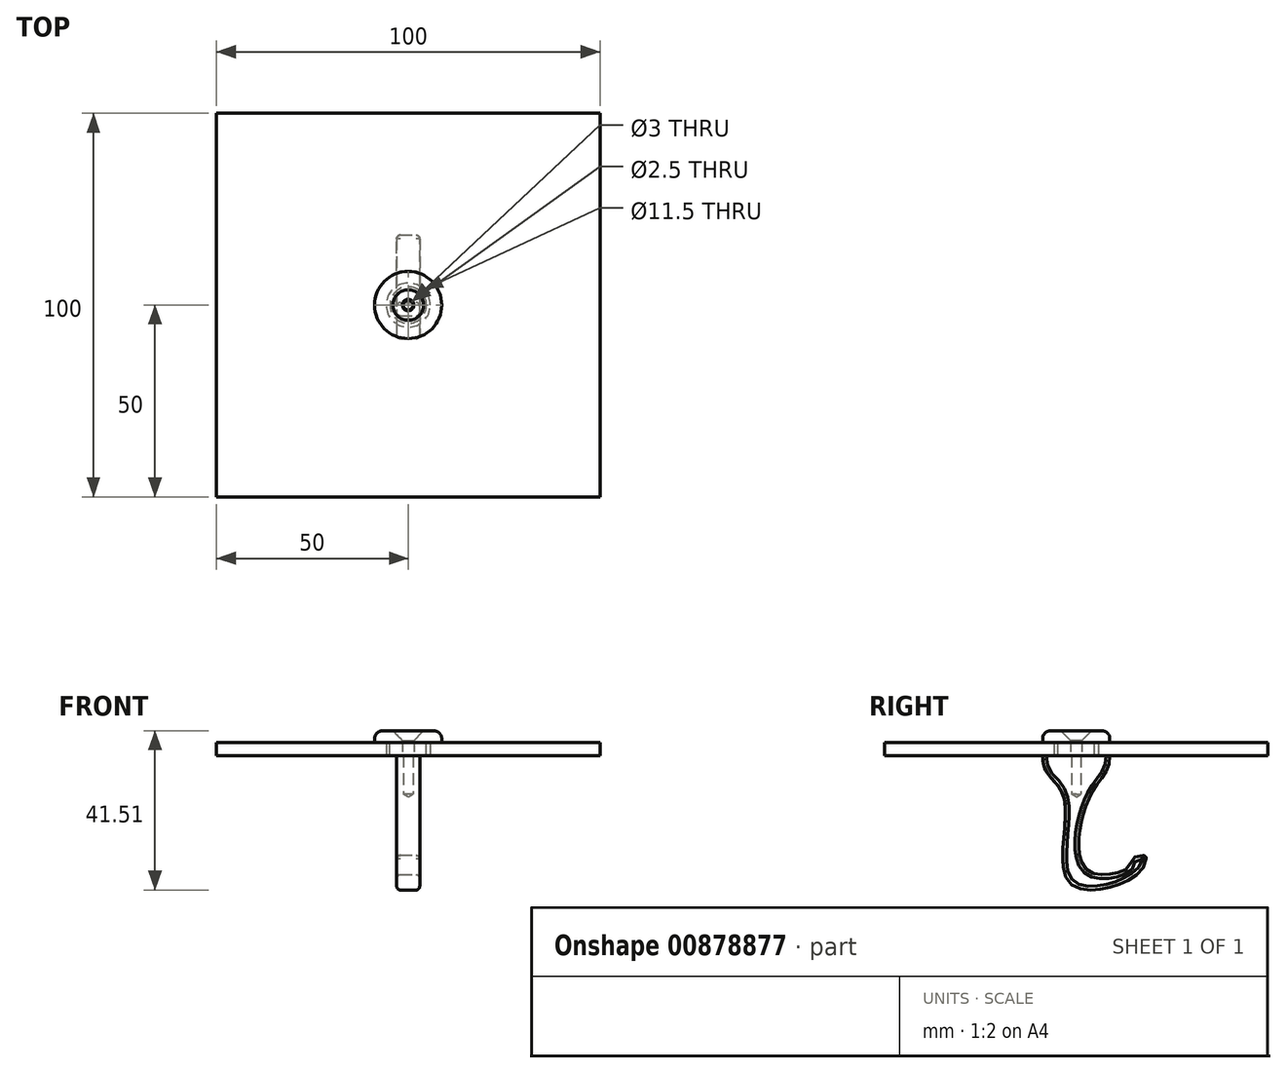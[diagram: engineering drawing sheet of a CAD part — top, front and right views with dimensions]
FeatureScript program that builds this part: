
annotation { "Feature Type Name" : "Feature", "Feature Type Description" : "" }
export const myFeature = defineFeature(function(context is Context, id is Id, definition is map)
    precondition{}
    {
        {
            var Q0;
            Q0=qCreatedBy(makeId("Top.planeOp"),FACE);
            var sketch = newSketch(context, id + "F0", { "sketchPlane" : qUnion([Q0])});
            skLineSegment(sketch, "E0.bottom", {"start": v(50, -50) * mm, "end": v(-50, -50) * mm});
            skLineSegment(sketch, "E0.top", {"start": v(50, 50) * mm, "end": v(-50, 50) * mm});
            skLineSegment(sketch, "E0.left", {"start": v(50, -50) * mm, "end": v(50, 50) * mm});
            skLineSegment(sketch, "E0.right", {"start": v(-50, -50) * mm, "end": v(-50, 50) * mm});
            skPoint(sketch, "E0.middle", {"position": v(0, 0) * mm});
            skCircle(sketch, "E1", {"center": v(0, 0) * mm, "radius": 5.75 * mm});
            skSolve(sketch);
        }
        {
            var Q0;
            Q0=makeQuery(id+"F0.imprint","IMPRINT",FACE,{"disambiguationData":[TD([[makeQuery(id+"F0.imprint","IMPRINT",EDGE,{"derivedFrom":sQuery(id+"F0.wireOp",EDGE,"E0.bottom")}),-1.0]])]});
            extrude(context, id + "F1", {"entities" : qUnion([Q0]), "depth" : 3.5 * mm, "offsetDistance" : 25 * mm});
        }
        {
            var Q0;
            Q0=makeQuery(id+"F1.opExtrude","CAP_FACE",FACE,{"disambiguationData":[OSD([sQuery(id+"F0.wireOp",EDGE,"E0.bottom"),sQuery(id+"F0.wireOp",EDGE,"E0.top"),sQuery(id+"F0.wireOp",EDGE,"E0.left"),sQuery(id+"F0.wireOp",EDGE,"E0.right"),sQuery(id+"F0.wireOp",EDGE,"E1")])],"isStart":false});
            var sketch = newSketch(context, id + "F2", { "sketchPlane" : qUnion([Q0])});
            skCircle(sketch, "E2", {"center": v(0, 0) * mm, "radius": 8.75 * mm});
            skSolve(sketch);
        }
        {
            var Q0;
            Q0=makeQuery(id+"F2.imprint","IMPRINT",FACE,{"disambiguationData":[TD([[makeQuery(id+"F2.imprint","IMPRINT",EDGE,{"derivedFrom":sQuery(id+"F2.wireOp",EDGE,"E2")}),1.0]])]});
            var Q1;
            Q1=makeQuery(id+"F2.imprint","IMPRINT",FACE,{"disambiguationData":[TD([[makeQuery(id+"F2.imprint","IMPRINT",EDGE,{"derivedFrom":makeQuery(id+"F1.opExtrude","CAP_EDGE",EDGE,{"disambiguationData":[OSD([sQuery(id+"F0.wireOp",EDGE,"E1")])],"isStart":false})}),1.0]])]});
            extrude(context, id + "F3", {"entities" : qUnion([Q0, Q1]), "depth" : 3 * mm, "offsetDistance" : 25 * mm});
        }
        {
            var Q0;
            Q0=makeQuery(id+"F3.opExtrude","CAP_FACE",FACE,{"disambiguationData":[OSD([sQuery(id+"F2.wireOp",EDGE,"E2")])],"isStart":true});
            var sketch = newSketch(context, id + "F4", { "sketchPlane" : qUnion([Q0])});
            skCircle(sketch, "E3.0", {"center": v(0, 0) * mm, "radius": 4.75 * mm});
            skSolve(sketch);
        }
        {
            var Q0;
            Q0=makeQuery(id+"F4.imprint","IMPRINT",FACE,{"disambiguationData":[TD([[makeQuery(id+"F4.imprint","IMPRINT",EDGE,{"derivedFrom":sQuery(id+"F4.wireOp",EDGE,"E3.0")}),1.0]])]});
            extrude(context, id + "F5", {"entities" : qUnion([Q0]), "operationType" : NewBodyOperationType.ADD, "depth" : 3.3 * mm, "offsetDistance" : 25 * mm});
        }
        {
            var Q0;
            Q0=makeQuery(id+"F3.opExtrude","CAP_EDGE",EDGE,{"disambiguationData":[OSD([sQuery(id+"F2.wireOp",EDGE,"E2")])],"isStart":false});
            fillet(context, id + "F6", {"entities" : qUnion([Q0]), "radius" : 2 * mm, "tangentPropagation" : true, "allowEdgeOverflow" : false});
        }
        {
            var Q0;
            Q0=makeQuery(id+"F3.opExtrude","CAP_FACE",FACE,{"disambiguationData":[OSD([sQuery(id+"F2.wireOp",EDGE,"E2")])],"isStart":false});
            var sketch = newSketch(context, id + "F7", { "sketchPlane" : qUnion([Q0])});
            skPoint(sketch, "E4", {"position": v(0, 0) * mm});
            skSolve(sketch);
        }
        {
            var Q0;
            Q0=sQuery(id+"F7.wireOp",VERTEX,"E4");
            var Q1;
            Q1=makeQuery(id+"F3.opExtrude","SWEPT_BODY",BODY,{"disambiguationData":[OSD([sQuery(id+"F2.wireOp",EDGE,"E2")])]});
            hole(context, id + "F8", {"style" : HoleStyle.C_SINK, "endStyle" : HoleEndStyle.THROUGH, "holeDiameter" : 3 * mm, "cSinkDiameter" : 8 * mm, "cSinkAngle" : 90 * degree, "majorDiameter" : 5 * mm, "isTappedThrough" : true, "tappedDepth" : 12 * mm, "tapClearance" : 3, "locations" : qUnion([Q0]), "scope" : qUnion([Q1]), "startStyle" : HoleStartStyle.SKETCH});
        }
        {
            var Q0;
            Q0=qCreatedBy(makeId("Right.planeOp"),FACE);
            var sketch = newSketch(context, id + "F9", { "sketchPlane" : qUnion([Q0])});
            skLineSegment(sketch, "E5", {"start": v(8.75, 0) * mm, "end": v(-8.75, 0) * mm});
            skLineSegment(sketch, "E6.0", {"start": v(-8.75, 3.5) * mm, "end": v(8.75, 3.5) * mm, "construction": true});
            skFitSpline(sketch, "E7", {"points": [v(8.75, 0) * mm, v(7.3, -4.9) * mm, v(2.97, -12) * mm, v(2.97, -29.9) * mm, v(13.79, -28.94) * mm, v(14.4, -27.1) * mm, v(17.8, -26.07) * mm, v(16.15, -30.66) * mm, v(-1.6, -33.27) * mm, v(-2.97, -12) * mm, v(-7.3, -4.9) * mm, v(-8.75, 0) * mm], "startDerivative": vector(3.16, -84.86) * mm, "endDerivative": vector(4.18, 84.8) * mm});
            skSolve(sketch);
        }
        {
            var Q0;
            Q0=makeQuery(id+"F9.imprint","IMPRINT",FACE,{"disambiguationData":[TD([[makeQuery(id+"F9.imprint","IMPRINT",EDGE,{"derivedFrom":sQuery(id+"F9.wireOp",EDGE,"E5")}),1.0]])]});
            extrude(context, id + "F10", {"entities" : qUnion([Q0]), "depth" : 6 * mm, "offsetDistance" : 25 * mm, "symmetric" : true});
        }
        {
            var Q0;
            Q0=makeQuery(id+"F10.opExtrude","SWEPT_FACE",FACE,{"disambiguationData":[OSD([sQuery(id+"F9.wireOp",EDGE,"E5")])]});
            var sketch = newSketch(context, id + "F11", { "sketchPlane" : qUnion([Q0])});
            skPoint(sketch, "E8", {"position": v(0, 0) * mm});
            skSolve(sketch);
        }
        {
            var Q0;
            Q0=sQuery(id+"F11.wireOp",VERTEX,"E8");
            var Q1;
            Q1=makeQuery(id+"F10.opExtrude","SWEPT_BODY",BODY,{"disambiguationData":[OSD([sQuery(id+"F9.wireOp",EDGE,"E5"),sQuery(id+"F9.wireOp",EDGE,"E7")])]});
            hole(context, id + "F12", {"style" : HoleStyle.SIMPLE, "endStyle" : HoleEndStyle.BLIND, "holeDiameter" : 2.5 * mm, "majorDiameter" : 5 * mm, "holeDepth" : 10 * mm, "isTappedThrough" : true, "tappedDepth" : 12 * mm, "tapClearance" : 3, "locations" : qUnion([Q0]), "scope" : qUnion([Q1]), "startStyle" : HoleStartStyle.SKETCH});
        }
        {
            var Q0;
            Q0=makeQuery(id+"F10.opExtrude","CAP_EDGE",EDGE,{"disambiguationData":[OSD([sQuery(id+"F9.wireOp",EDGE,"E7")])],"isStart":false});
            var Q1;
            Q1=makeQuery(id+"F10.opExtrude","CAP_EDGE",EDGE,{"disambiguationData":[OSD([sQuery(id+"F9.wireOp",EDGE,"E7")])],"isStart":true});
            fillet(context, id + "F13", {"entities" : qUnion([Q0, Q1]), "radius" : 1 * mm, "tangentPropagation" : true, "allowEdgeOverflow" : false});
        }
    });
